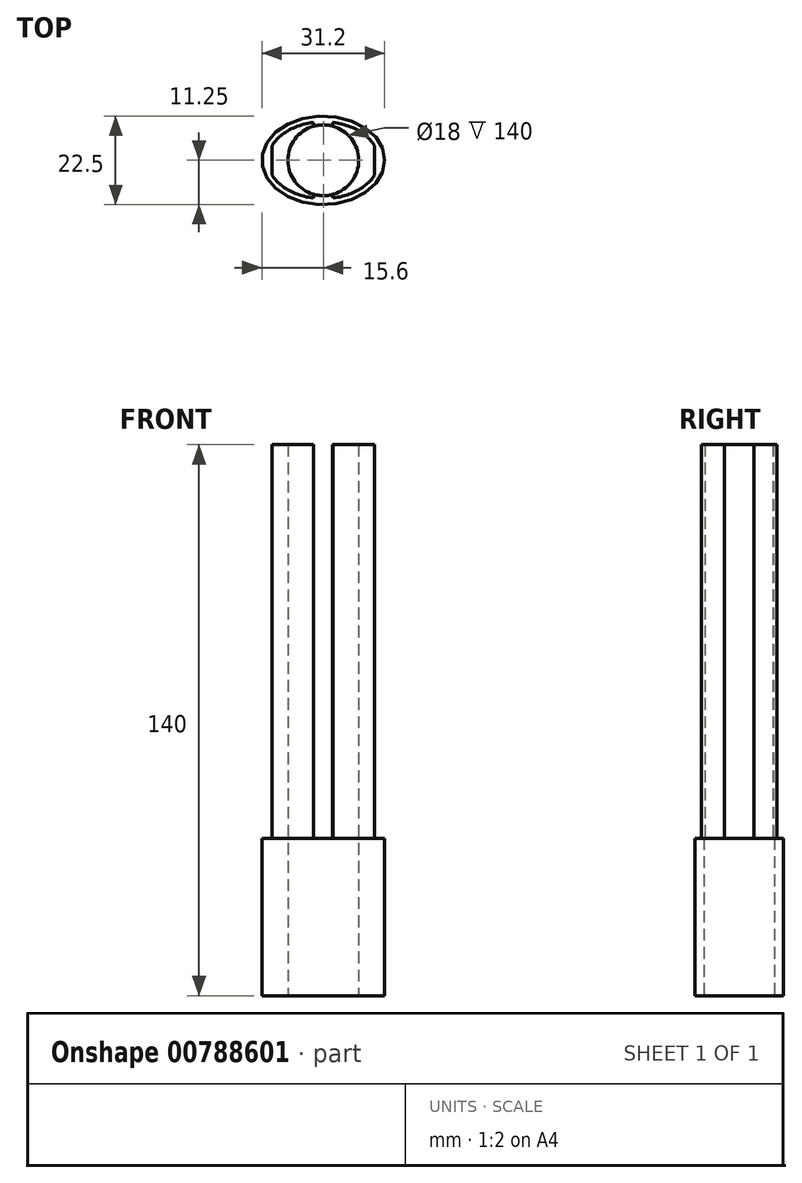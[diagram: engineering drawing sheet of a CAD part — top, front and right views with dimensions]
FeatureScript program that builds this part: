
annotation { "Feature Type Name" : "Feature", "Feature Type Description" : "" }
export const myFeature = defineFeature(function(context is Context, id is Id, definition is map)
    precondition{}
    {
        {
            var Q0;
            Q0=qCreatedBy(makeId("Top.planeOp"),FACE);
            var sketch = newSketch(context, id + "F0", { "sketchPlane" : qUnion([Q0])});
            skEllipse(sketch, "E0", {"center": v(0, 0) * mm, "majorRadius": 15.6 * mm, "minorRadius": 11.25 * mm, "majorAxis": v(1, 0)});
            skSolve(sketch);
        }
        {
            var Q0;
            Q0=qSketchRegion(id+"F0",true);
            extrude(context, id + "F1", {"entities" : qUnion([Q0]), "depth" : 40 * mm, "offsetDistance" : 25.4 * mm});
        }
        {
            var Q0;
            Q0=makeQuery(id+"F1.opExtrude","CAP_FACE",FACE,{"disambiguationData":[OSD([sQuery(id+"F0.wireOp",EDGE,"E0")])],"isStart":false});
            var sketch = newSketch(context, id + "F2", { "sketchPlane" : qUnion([Q0])});
            skEllipticalArc(sketch, "E1", {});
            skLineSegment(sketch, "E2", {"start": v(13, 3.78) * mm, "end": v(13, -3.78) * mm});
            skLineSegment(sketch, "E3", {"start": v(-13, 3.78) * mm, "end": v(-13, -3.78) * mm});
            skEllipticalArc(sketch, "E4.trimOffspring", {});
            skLineSegment(sketch, "E5", {"start": v(-2.5, 9.6) * mm, "end": v(-2.5, -9.6) * mm});
            skLineSegment(sketch, "E6", {"start": v(2.5, -9.6) * mm, "end": v(2.37, 9.61) * mm});
            skLineSegment(sketch, "E7", {"start": v(2.37, 9.61) * mm, "end": v(2.37, 9.61) * mm});
            skEllipticalArc(sketch, "E8.trimOffspring", {});
            skEllipticalArc(sketch, "E9.trimOffspring", {});
            const initialGuessF2  = {"E1": [0, 0, 1, 0, 0.0141, 0.00975, 0.3976184106167527, 1.402251659141812], "E4.trimOffspring": [0, 0, 1, 0, 0.0141, 0.00975, 3.5392110642065457, 4.534141631554835], "E8.trimOffspring": [0, 0, 1, 0, 0.0141, 0.00975, 1.7490436756247512, 2.743974242973041], "E9.trimOffspring": [0, 0, 1, 0, 0.0141, 0.00975, 4.890636329214544, 5.885566896562835]};
            skSetInitialGuess(sketch, initialGuessF2);
            skSolve(sketch);
        }
        {
            var Q0;
            Q0=qSketchRegion(id+"F2",true);
            extrude(context, id + "F3", {"entities" : qUnion([Q0]), "operationType" : NewBodyOperationType.ADD, "depth" : 100 * mm, "offsetDistance" : 25 * mm});
        }
        {
            var Q0;
            Q0=sQuery(id+"F0.wireOp",VERTEX,"E0.center");
            var Q1;
            Q1=makeQuery(id+"F1.opExtrude","SWEPT_BODY",BODY,{"disambiguationData":[OSD([sQuery(id+"F0.wireOp",EDGE,"E0")])]});
            hole(context, id + "F4", {"style" : HoleStyle.SIMPLE, "endStyle" : HoleEndStyle.THROUGH, "oppositeDirection" : true, "holeDiameter" : 18 * mm, "majorDiameter" : 5 * mm, "isTappedThrough" : true, "tappedDepth" : 12 * mm, "tapClearance" : 3, "locations" : qUnion([Q0]), "scope" : qUnion([Q1])});
        }
    });
